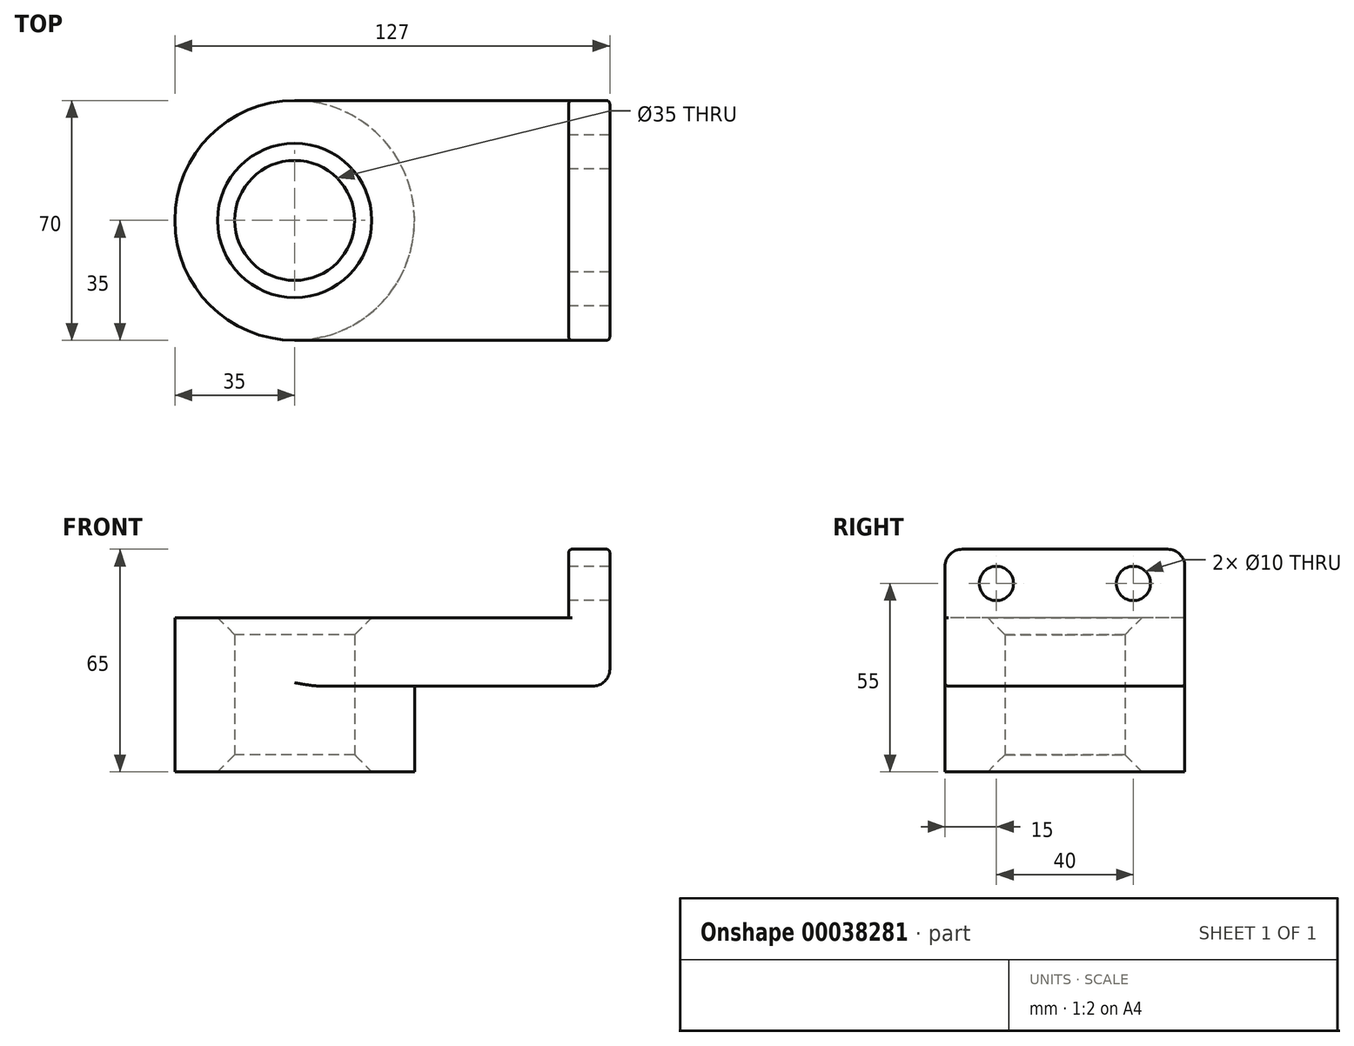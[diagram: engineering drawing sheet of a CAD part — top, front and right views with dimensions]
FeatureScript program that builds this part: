
annotation { "Feature Type Name" : "Feature", "Feature Type Description" : "" }
export const myFeature = defineFeature(function(context is Context, id is Id, definition is map)
    precondition{}
    {
        {
            var Q0;
            Q0=qCreatedBy(makeId("Top.planeOp"),FACE);
            var sketch = newSketch(context, id + "F0", { "sketchPlane" : qUnion([Q0])});
            skLineSegment(sketch, "E0.rect.bottom", {"start": v(-40, 35) * mm, "end": v(40, 35) * mm});
            skLineSegment(sketch, "E0.rect.top", {"start": v(-40, -35) * mm, "end": v(40, -35) * mm});
            skLineSegment(sketch, "E0.rect.left", {"start": v(-40, 35) * mm, "end": v(-40, -35) * mm});
            skLineSegment(sketch, "E0.rect.right", {"start": v(40, 35) * mm, "end": v(40, -35) * mm});
            skPoint(sketch, "E0.rect.middle", {"position": v(0, 0) * mm});
            skCircle(sketch, "E1", {"center": v(-40, 0) * mm, "radius": 35 * mm});
            skCircle(sketch, "E2", {"center": v(-40, 0) * mm, "radius": 17.5 * mm});
            skSolve(sketch);
        }
        {
            var Q0;
            {var subQ1=sQuery(id+"F0.wireOp",EDGE,"E0.rect.left");var subQ4=sQuery(id+"F0.wireOp",EDGE,"E1");var subQ6=makeQuery(id+"F0.imprint","INTERSECT",VERTEX,{"disambiguationData":[OD(0.0)],"derivedFrom":[subQ1,subQ4]});Q0=makeQuery(id+"F0.imprint","IMPRINT",FACE,{"disambiguationData":[TD([[makeQuery(id+"F0.imprint","IMPRINT",EDGE,{"disambiguationData":[TD([[subQ6,-1.0]])],"derivedFrom":subQ1}),1.0]])]});}
            var Q1;
            {var subQ0=sQuery(id+"F0.wireOp",EDGE,"E0.rect.bottom");Q1=makeQuery(id+"F0.imprint","IMPRINT",FACE,{"disambiguationData":[TD([[makeQuery(id+"F0.imprint","IMPRINT",EDGE,{"derivedFrom":subQ0}),-1.0]])]});}
            var Q2;
            {var subQ1=sQuery(id+"F0.wireOp",EDGE,"E0.rect.left");var subQ4=sQuery(id+"F0.wireOp",EDGE,"E1");var subQ6=makeQuery(id+"F0.imprint","INTERSECT",VERTEX,{"disambiguationData":[OD(0.0)],"derivedFrom":[subQ1,subQ4]});Q2=makeQuery(id+"F0.imprint","IMPRINT",FACE,{"disambiguationData":[TD([[makeQuery(id+"F0.imprint","IMPRINT",EDGE,{"disambiguationData":[TD([[subQ6,-1.0]])],"derivedFrom":subQ1}),-1.0]])]});}
            extrude(context, id + "F1", {"entities" : qUnion([Q0, Q1, Q2]), "depth" : 20 * mm});
        }
        {
            var Q0;
            {var subQ0=sQuery(id+"F0.wireOp",EDGE,"E2");var subQ1=sQuery(id+"F0.wireOp",EDGE,"E0.rect.left");var subQ3=makeQuery(id+"F0.imprint","INTERSECT",VERTEX,{"disambiguationData":[OD(0.0)],"derivedFrom":[subQ1,subQ0]});Q0=makeQuery(id+"F0.imprint","IMPRINT",FACE,{"disambiguationData":[TD([[makeQuery(id+"F0.imprint","IMPRINT",EDGE,{"disambiguationData":[TD([[subQ3,1.0]])],"derivedFrom":subQ0}),-1.0]])]});}
            var Q1;
            {var subQ0=sQuery(id+"F0.wireOp",EDGE,"E2");var subQ1=sQuery(id+"F0.wireOp",EDGE,"E0.rect.left");var subQ3=makeQuery(id+"F0.imprint","INTERSECT",VERTEX,{"disambiguationData":[OD(0.0)],"derivedFrom":[subQ1,subQ0]});Q1=makeQuery(id+"F0.imprint","IMPRINT",FACE,{"disambiguationData":[TD([[makeQuery(id+"F0.imprint","IMPRINT",EDGE,{"disambiguationData":[TD([[subQ3,-1.0]])],"derivedFrom":subQ0}),-1.0]])]});}
            extrude(context, id + "F2", {"entities" : qUnion([Q0, Q1]), "operationType" : NewBodyOperationType.ADD, "oppositeDirection" : true, "depth" : 25 * mm});
        }
        {
            var Q0;
            Q0=makeQuery(id+"F1.opExtrude","SWEPT_FACE",FACE,{"disambiguationData":[OSD([sQuery(id+"F0.wireOp",EDGE,"E0.rect.right")])]});
            var sketch = newSketch(context, id + "F3", { "sketchPlane" : qUnion([Q0])});
            skLineSegment(sketch, "E3.bottom", {"start": v(-35, 0) * mm, "end": v(35, 0) * mm});
            skLineSegment(sketch, "E3.top", {"start": v(-35, 40) * mm, "end": v(35, 40) * mm});
            skLineSegment(sketch, "E3.left", {"start": v(-35, 0) * mm, "end": v(-35, 40) * mm});
            skLineSegment(sketch, "E3.right", {"start": v(35, 0) * mm, "end": v(35, 40) * mm});
            skLineSegment(sketch, "E4", {"start": v(0, 0) * mm, "end": v(0, 57.96) * mm, "construction": true});
            skCircle(sketch, "E5", {"center": v(-20, 30) * mm, "radius": 5 * mm});
            skCircle(sketch, "E6.MirrorC", {"center": v(20, 30) * mm, "radius": 5 * mm});
            skSolve(sketch);
        }
        {
            var Q0;
            {var subQ1=sQuery(id+"F3.wireOp",EDGE,"E3.top");Q0=makeQuery(id+"F3.imprint","IMPRINT",FACE,{"disambiguationData":[TD([[makeQuery(id+"F3.imprint","IMPRINT",EDGE,{"derivedFrom":subQ1}),-1.0]])]});}
            var Q1;
            {var subQ2=sQuery(id+"F3.wireOp",EDGE,"E3.bottom");Q1=makeQuery(id+"F3.imprint","IMPRINT",FACE,{"disambiguationData":[TD([[makeQuery(id+"F3.imprint","IMPRINT",EDGE,{"derivedFrom":subQ2}),-1.0]])]});}
            extrude(context, id + "F4", {"entities" : qUnion([Q0, Q1]), "operationType" : NewBodyOperationType.ADD, "depth" : 12 * mm});
        }
        {
            var Q0;
            Q0=makeQuery(id+"F4.opExtrude","SWEPT_EDGE",EDGE,{"disambiguationData":[OSD([sQuery(id+"F3.wireOp",EDGE,"E3.top"),sQuery(id+"F3.wireOp",EDGE,"E3.right")])]});
            var Q1;
            Q1=makeQuery(id+"F4.opExtrude","SWEPT_EDGE",EDGE,{"disambiguationData":[OSD([sQuery(id+"F3.wireOp",EDGE,"E3.top"),sQuery(id+"F3.wireOp",EDGE,"E3.left")])]});
            var Q2;
            Q2=makeQuery(id+"F4.opExtrude","CAP_EDGE",EDGE,{"disambiguationData":[OSD([sQuery(id+"F3.wireOp",EDGE,"E3.bottom")])],"isStart":false});
            var Q3;
            Q3=makeQuery(id+"F2.opExtrude","CAP_EDGE",EDGE,{"disambiguationData":[OSD([sQuery(id+"F0.wireOp",EDGE,"E1")])],"isStart":true});
            fillet(context, id + "F5", {"entities" : qUnion([Q0, Q1, Q2, Q3]), "radius" : 5 * mm, "tangentPropagation" : true, "allowEdgeOverflow" : false});
        }
        {
            var Q0;
            {var subQ0=sQuery(id+"F0.wireOp",EDGE,"E2");Q0=makeQuery(id+"F2.boolean.opBoolean","MERGE",FACE,{"derivedFrom":[makeQuery(id+"F1.opExtrude","SWEPT_FACE",FACE,{"disambiguationData":[OSD([subQ0])]}),makeQuery(id+"F2.opExtrude","SWEPT_FACE",FACE,{"disambiguationData":[OSD([subQ0])]})]});}
            chamfer(context, id + "F6", {"entities" : qUnion([Q0]), "chamferType" : ChamferType.OFFSET_ANGLE, "width" : 5 * mm, "oppositeDirection" : false, "angle" : 45 * degree, "tangentPropagation" : true});
        }
        {
            var Q0;
            Q0=makeQuery(id+"F1.opExtrude","CAP_EDGE",EDGE,{"disambiguationData":[OSD([sQuery(id+"F0.wireOp",EDGE,"E0.rect.right")])],"isStart":false});
            var Q1;
            Q1=makeQuery(id+"F4.opExtrude","CAP_EDGE",EDGE,{"disambiguationData":[OSD([sQuery(id+"F3.wireOp",EDGE,"E3.top")])],"isStart":true});
            var Q2;
            Q2=makeQuery(id+"F4.opExtrude","CAP_EDGE",EDGE,{"disambiguationData":[OSD([sQuery(id+"F3.wireOp",EDGE,"E3.top")])],"isStart":false});
            fillet(context, id + "F7", {"entities" : qUnion([Q0, Q1, Q2]), "radius" : 1 * mm, "tangentPropagation" : true, "allowEdgeOverflow" : false});
        }
    });
